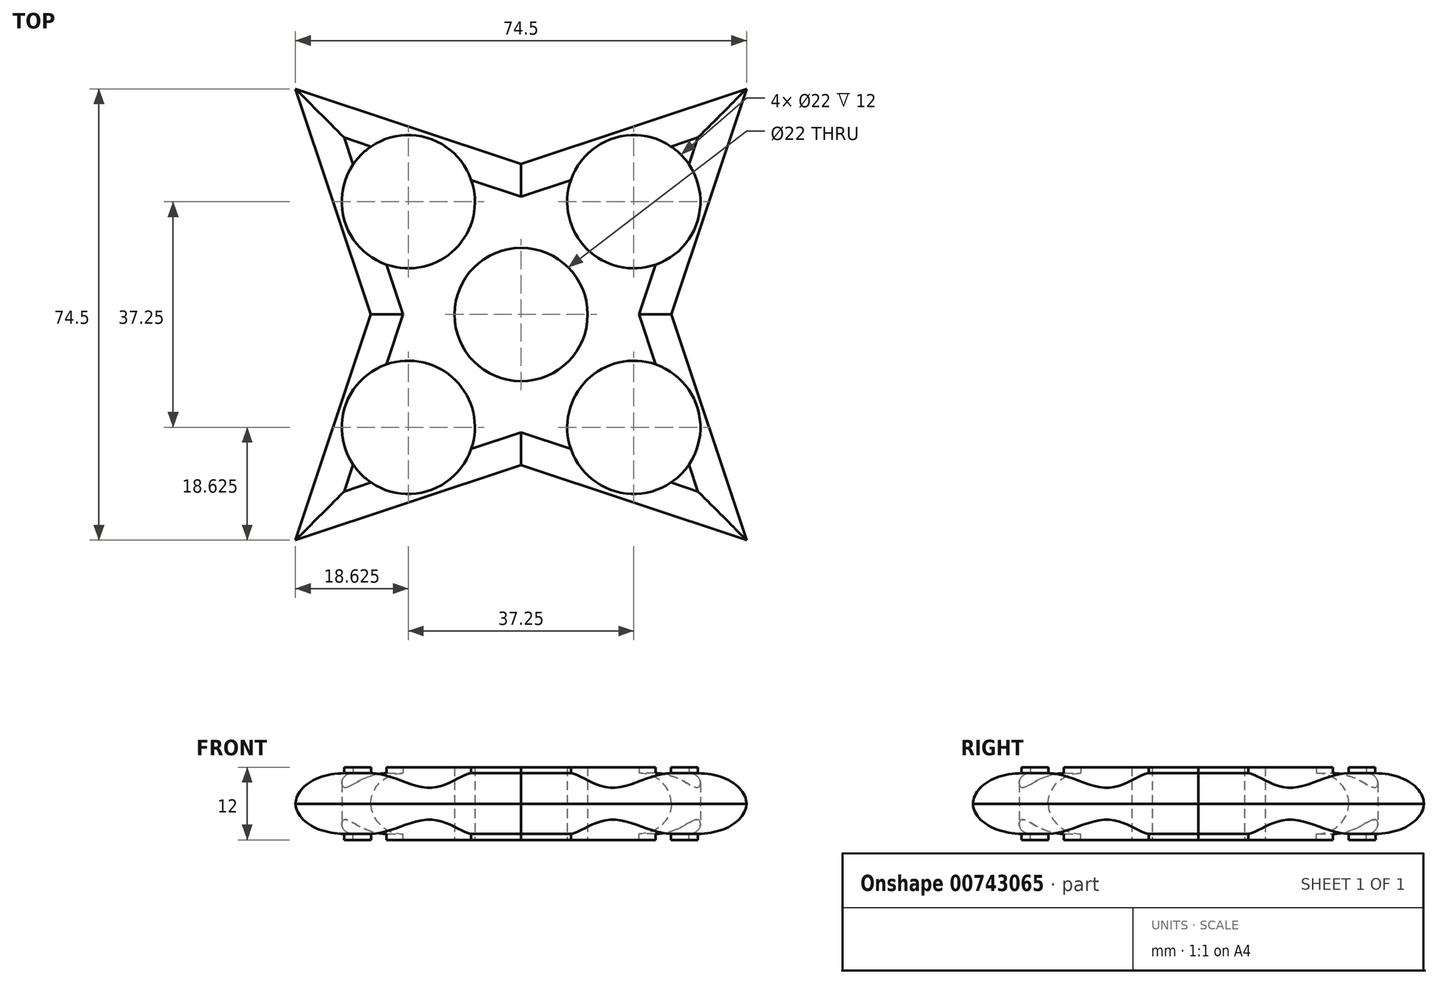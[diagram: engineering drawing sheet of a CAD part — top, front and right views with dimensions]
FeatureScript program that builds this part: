
annotation { "Feature Type Name" : "Feature", "Feature Type Description" : "" }
export const myFeature = defineFeature(function(context is Context, id is Id, definition is map)
    precondition{}
    {
        {
            var Q0;
            Q0=qCreatedBy(makeId("Top.planeOp"),FACE);
            var sketch = newSketch(context, id + "F0", { "sketchPlane" : qUnion([Q0])});
            skLineSegment(sketch, "E0.bottom", {"start": v(-109.63, 111.87) * mm, "end": v(113.44, 111.87) * mm});
            skLineSegment(sketch, "E0.top", {"start": v(-109.63, -97) * mm, "end": v(113.44, -97) * mm});
            skLineSegment(sketch, "E0.left", {"start": v(-109.63, 111.87) * mm, "end": v(-109.63, -97) * mm});
            skLineSegment(sketch, "E0.right", {"start": v(113.44, 111.87) * mm, "end": v(113.44, -97) * mm});
            skCircle(sketch, "E1", {"center": v(0, 0) * mm, "radius": 11 * mm});
            skLineSegment(sketch, "E2", {"start": v(0, 11) * mm, "end": v(0, 74.5) * mm});
            skLineSegment(sketch, "E3", {"start": v(11, 0) * mm, "end": v(74.5, 0) * mm});
            skLineSegment(sketch, "E4", {"start": v(0, -11) * mm, "end": v(0, -74.5) * mm});
            skLineSegment(sketch, "E5", {"start": v(-11, 0) * mm, "end": v(-74.5, 0) * mm});
            skLineSegment(sketch, "E6", {"start": v(37.25, 37.25) * mm, "end": v(-37.25, -37.25) * mm});
            skLineSegment(sketch, "E7", {"start": v(-37.25, 37.25) * mm, "end": v(37.25, -37.25) * mm});
            skLineSegment(sketch, "E8", {"start": v(37.25, 37.25) * mm, "end": v(0, -74.5) * mm});
            skLineSegment(sketch, "E9", {"start": v(-37.25, 37.25) * mm, "end": v(0, -74.5) * mm});
            skLineSegment(sketch, "E10", {"start": v(-74.5, 0) * mm, "end": v(37.25, 37.25) * mm});
            skLineSegment(sketch, "E11", {"start": v(37.25, -37.25) * mm, "end": v(-74.5, 0) * mm});
            skLineSegment(sketch, "E12", {"start": v(-37.25, -37.25) * mm, "end": v(0, 74.5) * mm});
            skLineSegment(sketch, "E13", {"start": v(37.25, -37.25) * mm, "end": v(0, 74.5) * mm});
            skLineSegment(sketch, "E14", {"start": v(-37.25, -37.25) * mm, "end": v(74.5, 0) * mm});
            skLineSegment(sketch, "E15", {"start": v(-37.25, 37.25) * mm, "end": v(74.5, 0) * mm});
            skCircle(sketch, "E16", {"center": v(-18.62, 18.62) * mm, "radius": 11 * mm});
            skCircle(sketch, "E17", {"center": v(18.63, 18.62) * mm, "radius": 11 * mm});
            skCircle(sketch, "E18", {"center": v(18.63, -18.62) * mm, "radius": 11 * mm});
            skCircle(sketch, "E19", {"center": v(-18.62, -18.62) * mm, "radius": 11 * mm});
            skSolve(sketch);
        }
        {
            var Q0;
            {var subQ0=sQuery(id+"F0.wireOp",EDGE,"E11");var subQ1=sQuery(id+"F0.wireOp",EDGE,"E8");var subQ2=makeQuery(id+"F0.imprint","INTERSECT",VERTEX,{"derivedFrom":[subQ1,subQ0]});Q0=makeQuery(id+"F0.imprint","IMPRINT",FACE,{"disambiguationData":[TD([[makeQuery(id+"F0.imprint","IMPRINT",EDGE,{"disambiguationData":[TD([[subQ2,1.0]])],"derivedFrom":subQ1}),-1.0]])]});}
            var Q1;
            {var subQ0=sQuery(id+"F0.wireOp",EDGE,"E14");var subQ1=sQuery(id+"F0.wireOp",EDGE,"E9");var subQ2=makeQuery(id+"F0.imprint","INTERSECT",VERTEX,{"derivedFrom":[subQ1,subQ0]});Q1=makeQuery(id+"F0.imprint","IMPRINT",FACE,{"disambiguationData":[TD([[makeQuery(id+"F0.imprint","IMPRINT",EDGE,{"disambiguationData":[TD([[subQ2,1.0]])],"derivedFrom":subQ1}),1.0]])]});}
            var Q2;
            {var subQ0=sQuery(id+"F0.wireOp",EDGE,"E4");var subQ1=sQuery(id+"F0.wireOp",EDGE,"E1");var subQ2=makeQuery(id+"F0.imprint","INTERSECT",VERTEX,{"derivedFrom":[subQ1,subQ0]});Q2=makeQuery(id+"F0.imprint","IMPRINT",FACE,{"disambiguationData":[TD([[makeQuery(id+"F0.imprint","IMPRINT",EDGE,{"disambiguationData":[TD([[subQ2,1.0]])],"derivedFrom":subQ1}),-1.0]])]});}
            var Q3;
            {var subQ0=sQuery(id+"F0.wireOp",EDGE,"E5");var subQ1=sQuery(id+"F0.wireOp",EDGE,"E1");var subQ2=makeQuery(id+"F0.imprint","INTERSECT",VERTEX,{"derivedFrom":[subQ1,subQ0]});Q3=makeQuery(id+"F0.imprint","IMPRINT",FACE,{"disambiguationData":[TD([[makeQuery(id+"F0.imprint","IMPRINT",EDGE,{"disambiguationData":[TD([[subQ2,-1.0]])],"derivedFrom":subQ1}),-1.0]])]});}
            var Q4;
            {var subQ0=sQuery(id+"F0.wireOp",EDGE,"E5");var subQ1=sQuery(id+"F0.wireOp",EDGE,"E1");var subQ2=makeQuery(id+"F0.imprint","INTERSECT",VERTEX,{"derivedFrom":[subQ1,subQ0]});Q4=makeQuery(id+"F0.imprint","IMPRINT",FACE,{"disambiguationData":[TD([[makeQuery(id+"F0.imprint","IMPRINT",EDGE,{"disambiguationData":[TD([[subQ2,1.0]])],"derivedFrom":subQ1}),-1.0]])]});}
            var Q5;
            {var subQ0=sQuery(id+"F0.wireOp",EDGE,"E2");var subQ1=sQuery(id+"F0.wireOp",EDGE,"E1");var subQ2=makeQuery(id+"F0.imprint","INTERSECT",VERTEX,{"derivedFrom":[subQ1,subQ0]});Q5=makeQuery(id+"F0.imprint","IMPRINT",FACE,{"disambiguationData":[TD([[makeQuery(id+"F0.imprint","IMPRINT",EDGE,{"disambiguationData":[TD([[subQ2,-1.0]])],"derivedFrom":subQ1}),-1.0]])]});}
            var Q6;
            {var subQ0=sQuery(id+"F0.wireOp",EDGE,"E2");var subQ1=sQuery(id+"F0.wireOp",EDGE,"E1");var subQ2=makeQuery(id+"F0.imprint","INTERSECT",VERTEX,{"derivedFrom":[subQ1,subQ0]});Q6=makeQuery(id+"F0.imprint","IMPRINT",FACE,{"disambiguationData":[TD([[makeQuery(id+"F0.imprint","IMPRINT",EDGE,{"disambiguationData":[TD([[subQ2,1.0]])],"derivedFrom":subQ1}),-1.0]])]});}
            var Q7;
            {var subQ0=sQuery(id+"F0.wireOp",EDGE,"E3");var subQ1=sQuery(id+"F0.wireOp",EDGE,"E1");var subQ2=makeQuery(id+"F0.imprint","INTERSECT",VERTEX,{"derivedFrom":[subQ1,subQ0]});Q7=makeQuery(id+"F0.imprint","IMPRINT",FACE,{"disambiguationData":[TD([[makeQuery(id+"F0.imprint","IMPRINT",EDGE,{"disambiguationData":[TD([[subQ2,-1.0]])],"derivedFrom":subQ1}),-1.0]])]});}
            var Q8;
            {var subQ0=sQuery(id+"F0.wireOp",EDGE,"E3");var subQ1=sQuery(id+"F0.wireOp",EDGE,"E1");var subQ2=makeQuery(id+"F0.imprint","INTERSECT",VERTEX,{"derivedFrom":[subQ1,subQ0]});Q8=makeQuery(id+"F0.imprint","IMPRINT",FACE,{"disambiguationData":[TD([[makeQuery(id+"F0.imprint","IMPRINT",EDGE,{"disambiguationData":[TD([[subQ2,1.0]])],"derivedFrom":subQ1}),-1.0]])]});}
            var Q9;
            {var subQ0=sQuery(id+"F0.wireOp",EDGE,"E4");var subQ1=sQuery(id+"F0.wireOp",EDGE,"E1");var subQ2=makeQuery(id+"F0.imprint","INTERSECT",VERTEX,{"derivedFrom":[subQ1,subQ0]});Q9=makeQuery(id+"F0.imprint","IMPRINT",FACE,{"disambiguationData":[TD([[makeQuery(id+"F0.imprint","IMPRINT",EDGE,{"disambiguationData":[TD([[subQ2,-1.0]])],"derivedFrom":subQ1}),-1.0]])]});}
            var Q10;
            {var subQ0=sQuery(id+"F0.wireOp",EDGE,"E13");var subQ3=sQuery(id+"F0.wireOp",EDGE,"E14");var subQ5=makeQuery(id+"F0.imprint","INTERSECT",VERTEX,{"derivedFrom":[subQ0,subQ3]});Q10=makeQuery(id+"F0.imprint","IMPRINT",FACE,{"disambiguationData":[TD([[makeQuery(id+"F0.imprint","IMPRINT",EDGE,{"disambiguationData":[TD([[subQ5,-1.0]])],"derivedFrom":subQ0}),1.0]])]});}
            var Q11;
            {var subQ0=sQuery(id+"F0.wireOp",EDGE,"E15");var subQ1=sQuery(id+"F0.wireOp",EDGE,"E8");var subQ2=makeQuery(id+"F0.imprint","INTERSECT",VERTEX,{"derivedFrom":[subQ1,subQ0]});Q11=makeQuery(id+"F0.imprint","IMPRINT",FACE,{"disambiguationData":[TD([[makeQuery(id+"F0.imprint","IMPRINT",EDGE,{"disambiguationData":[TD([[subQ2,-1.0]])],"derivedFrom":subQ1}),-1.0]])]});}
            var Q12;
            {var subQ0=sQuery(id+"F0.wireOp",EDGE,"E15");var subQ3=sQuery(id+"F0.wireOp",EDGE,"E12");var subQ5=makeQuery(id+"F0.imprint","INTERSECT",VERTEX,{"derivedFrom":[subQ3,subQ0]});Q12=makeQuery(id+"F0.imprint","IMPRINT",FACE,{"disambiguationData":[TD([[makeQuery(id+"F0.imprint","IMPRINT",EDGE,{"disambiguationData":[TD([[subQ5,1.0]])],"derivedFrom":subQ3}),-1.0]])]});}
            var Q13;
            {var subQ0=sQuery(id+"F0.wireOp",EDGE,"E13");var subQ1=sQuery(id+"F0.wireOp",EDGE,"E10");var subQ2=makeQuery(id+"F0.imprint","INTERSECT",VERTEX,{"derivedFrom":[subQ1,subQ0]});Q13=makeQuery(id+"F0.imprint","IMPRINT",FACE,{"disambiguationData":[TD([[makeQuery(id+"F0.imprint","IMPRINT",EDGE,{"disambiguationData":[TD([[subQ2,1.0]])],"derivedFrom":subQ1}),-1.0]])]});}
            var Q14;
            {var subQ0=sQuery(id+"F0.wireOp",EDGE,"E10");var subQ3=sQuery(id+"F0.wireOp",EDGE,"E13");var subQ5=makeQuery(id+"F0.imprint","INTERSECT",VERTEX,{"derivedFrom":[subQ0,subQ3]});Q14=makeQuery(id+"F0.imprint","IMPRINT",FACE,{"disambiguationData":[TD([[makeQuery(id+"F0.imprint","IMPRINT",EDGE,{"disambiguationData":[TD([[subQ5,-1.0]])],"derivedFrom":subQ0}),-1.0]])]});}
            var Q15;
            {var subQ0=sQuery(id+"F0.wireOp",EDGE,"E8");var subQ3=sQuery(id+"F0.wireOp",EDGE,"E15");var subQ5=makeQuery(id+"F0.imprint","INTERSECT",VERTEX,{"derivedFrom":[subQ0,subQ3]});Q15=makeQuery(id+"F0.imprint","IMPRINT",FACE,{"disambiguationData":[TD([[makeQuery(id+"F0.imprint","IMPRINT",EDGE,{"disambiguationData":[TD([[subQ5,1.0]])],"derivedFrom":subQ0}),-1.0]])]});}
            var Q16;
            {var subQ0=sQuery(id+"F0.wireOp",EDGE,"E11");var subQ3=sQuery(id+"F0.wireOp",EDGE,"E8");var subQ5=makeQuery(id+"F0.imprint","INTERSECT",VERTEX,{"derivedFrom":[subQ3,subQ0]});Q16=makeQuery(id+"F0.imprint","IMPRINT",FACE,{"disambiguationData":[TD([[makeQuery(id+"F0.imprint","IMPRINT",EDGE,{"disambiguationData":[TD([[subQ5,1.0]])],"derivedFrom":subQ3}),1.0]])]});}
            var Q17;
            {var subQ0=sQuery(id+"F0.wireOp",EDGE,"E13");var subQ3=sQuery(id+"F0.wireOp",EDGE,"E14");var subQ5=makeQuery(id+"F0.imprint","INTERSECT",VERTEX,{"derivedFrom":[subQ0,subQ3]});Q17=makeQuery(id+"F0.imprint","IMPRINT",FACE,{"disambiguationData":[TD([[makeQuery(id+"F0.imprint","IMPRINT",EDGE,{"disambiguationData":[TD([[subQ5,1.0]])],"derivedFrom":subQ0}),1.0]])]});}
            var Q18;
            {var subQ0=sQuery(id+"F0.wireOp",EDGE,"E14");var subQ3=sQuery(id+"F0.wireOp",EDGE,"E9");var subQ5=makeQuery(id+"F0.imprint","INTERSECT",VERTEX,{"derivedFrom":[subQ3,subQ0]});Q18=makeQuery(id+"F0.imprint","IMPRINT",FACE,{"disambiguationData":[TD([[makeQuery(id+"F0.imprint","IMPRINT",EDGE,{"disambiguationData":[TD([[subQ5,1.0]])],"derivedFrom":subQ3}),-1.0]])]});}
            var Q19;
            {var subQ0=sQuery(id+"F0.wireOp",EDGE,"E12");var subQ3=sQuery(id+"F0.wireOp",EDGE,"E11");var subQ5=makeQuery(id+"F0.imprint","INTERSECT",VERTEX,{"derivedFrom":[subQ3,subQ0]});Q19=makeQuery(id+"F0.imprint","IMPRINT",FACE,{"disambiguationData":[TD([[makeQuery(id+"F0.imprint","IMPRINT",EDGE,{"disambiguationData":[TD([[subQ5,1.0]])],"derivedFrom":subQ3}),-1.0]])]});}
            var Q20;
            {var subQ0=sQuery(id+"F0.wireOp",EDGE,"E12");var subQ3=sQuery(id+"F0.wireOp",EDGE,"E11");var subQ5=makeQuery(id+"F0.imprint","INTERSECT",VERTEX,{"derivedFrom":[subQ3,subQ0]});Q20=makeQuery(id+"F0.imprint","IMPRINT",FACE,{"disambiguationData":[TD([[makeQuery(id+"F0.imprint","IMPRINT",EDGE,{"disambiguationData":[TD([[subQ5,1.0]])],"derivedFrom":subQ3}),1.0]])]});}
            var Q21;
            {var subQ0=sQuery(id+"F0.wireOp",EDGE,"E10");var subQ1=sQuery(id+"F0.wireOp",EDGE,"E9");var subQ2=makeQuery(id+"F0.imprint","INTERSECT",VERTEX,{"derivedFrom":[subQ1,subQ0]});Q21=makeQuery(id+"F0.imprint","IMPRINT",FACE,{"disambiguationData":[TD([[makeQuery(id+"F0.imprint","IMPRINT",EDGE,{"disambiguationData":[TD([[subQ2,-1.0]])],"derivedFrom":subQ1}),1.0]])]});}
            var Q22;
            {var subQ0=sQuery(id+"F0.wireOp",EDGE,"E9");var subQ3=sQuery(id+"F0.wireOp",EDGE,"E10");var subQ5=makeQuery(id+"F0.imprint","INTERSECT",VERTEX,{"derivedFrom":[subQ0,subQ3]});Q22=makeQuery(id+"F0.imprint","IMPRINT",FACE,{"disambiguationData":[TD([[makeQuery(id+"F0.imprint","IMPRINT",EDGE,{"disambiguationData":[TD([[subQ5,1.0]])],"derivedFrom":subQ0}),1.0]])]});}
            var Q23;
            {var subQ0=sQuery(id+"F0.wireOp",EDGE,"E15");var subQ3=sQuery(id+"F0.wireOp",EDGE,"E12");var subQ5=makeQuery(id+"F0.imprint","INTERSECT",VERTEX,{"derivedFrom":[subQ3,subQ0]});Q23=makeQuery(id+"F0.imprint","IMPRINT",FACE,{"disambiguationData":[TD([[makeQuery(id+"F0.imprint","IMPRINT",EDGE,{"disambiguationData":[TD([[subQ5,1.0]])],"derivedFrom":subQ3}),1.0]])]});}
            extrude(context, id + "F1", {"entities" : qUnion([Q0, Q1, Q2, Q3, Q4, Q5, Q6, Q7, Q8, Q9, Q10, Q11, Q12, Q13, Q14, Q15, Q16, Q17, Q18, Q19, Q20, Q21, Q22, Q23]), "depth" : 10 * mm, "offsetDistance" : 25.4 * mm});
        }
        {
            var Q0;
            Q0=makeQuery(id+"F1.opExtrude","CAP_EDGE",EDGE,{"disambiguationData":[OSD([sQuery(id+"F0.wireOp",EDGE,"E12")])],"isStart":false});
            var Q1;
            Q1=makeQuery(id+"F1.opExtrude","CAP_EDGE",EDGE,{"disambiguationData":[OSD([sQuery(id+"F0.wireOp",EDGE,"E9")])],"isStart":false});
            var Q2;
            Q2=makeQuery(id+"F1.opExtrude","CAP_EDGE",EDGE,{"disambiguationData":[OSD([sQuery(id+"F0.wireOp",EDGE,"E14")])],"isStart":false});
            var Q3;
            Q3=makeQuery(id+"F1.opExtrude","CAP_EDGE",EDGE,{"disambiguationData":[OSD([sQuery(id+"F0.wireOp",EDGE,"E11")])],"isStart":false});
            var Q4;
            Q4=makeQuery(id+"F1.opExtrude","CAP_EDGE",EDGE,{"disambiguationData":[OSD([sQuery(id+"F0.wireOp",EDGE,"E13")])],"isStart":false});
            var Q5;
            Q5=makeQuery(id+"F1.opExtrude","CAP_EDGE",EDGE,{"disambiguationData":[OSD([sQuery(id+"F0.wireOp",EDGE,"E8")])],"isStart":false});
            var Q6;
            Q6=makeQuery(id+"F1.opExtrude","CAP_EDGE",EDGE,{"disambiguationData":[OSD([sQuery(id+"F0.wireOp",EDGE,"E10")])],"isStart":false});
            var Q7;
            Q7=makeQuery(id+"F1.opExtrude","CAP_EDGE",EDGE,{"disambiguationData":[OSD([sQuery(id+"F0.wireOp",EDGE,"E15")])],"isStart":false});
            fillet(context, id + "F2", {"entities" : qUnion([Q0, Q1, Q2, Q3, Q4, Q5, Q6, Q7]), "radius" : 5.08 * mm, "tangentPropagation" : true, "allowEdgeOverflow" : false});
        }
        {
            var Q0;
            Q0=makeQuery(id+"F1.opExtrude","CAP_EDGE",EDGE,{"disambiguationData":[OSD([sQuery(id+"F0.wireOp",EDGE,"E10")])],"isStart":true});
            var Q1;
            Q1=makeQuery(id+"F1.opExtrude","CAP_EDGE",EDGE,{"disambiguationData":[OSD([sQuery(id+"F0.wireOp",EDGE,"E8")])],"isStart":true});
            var Q2;
            Q2=makeQuery(id+"F1.opExtrude","CAP_EDGE",EDGE,{"disambiguationData":[OSD([sQuery(id+"F0.wireOp",EDGE,"E13")])],"isStart":true});
            var Q3;
            Q3=makeQuery(id+"F1.opExtrude","CAP_EDGE",EDGE,{"disambiguationData":[OSD([sQuery(id+"F0.wireOp",EDGE,"E11")])],"isStart":true});
            var Q4;
            Q4=makeQuery(id+"F1.opExtrude","CAP_EDGE",EDGE,{"disambiguationData":[OSD([sQuery(id+"F0.wireOp",EDGE,"E14")])],"isStart":true});
            var Q5;
            Q5=makeQuery(id+"F1.opExtrude","CAP_EDGE",EDGE,{"disambiguationData":[OSD([sQuery(id+"F0.wireOp",EDGE,"E12")])],"isStart":true});
            var Q6;
            Q6=makeQuery(id+"F1.opExtrude","CAP_EDGE",EDGE,{"disambiguationData":[OSD([sQuery(id+"F0.wireOp",EDGE,"E9")])],"isStart":true});
            var Q7;
            Q7=makeQuery(id+"F1.opExtrude","CAP_EDGE",EDGE,{"disambiguationData":[OSD([sQuery(id+"F0.wireOp",EDGE,"E15")])],"isStart":true});
            fillet(context, id + "F3", {"entities" : qUnion([Q0, Q1, Q2, Q3, Q4, Q5, Q6, Q7]), "radius" : 5.08 * mm, "tangentPropagation" : true, "allowEdgeOverflow" : false});
        }
        {
            var Q0;
            Q0=makeQuery(id+"F2.opFillet","SPLIT",FACE,{"disambiguationData":[OD(2.0)],"derivedFrom":makeQuery(id+"F1.opExtrude","CAP_FACE",FACE,{"disambiguationData":[OSD([sQuery(id+"F0.wireOp",EDGE,"E1"),sQuery(id+"F0.wireOp",EDGE,"E8"),sQuery(id+"F0.wireOp",EDGE,"E9"),sQuery(id+"F0.wireOp",EDGE,"E10"),sQuery(id+"F0.wireOp",EDGE,"E11"),sQuery(id+"F0.wireOp",EDGE,"E12"),sQuery(id+"F0.wireOp",EDGE,"E13"),sQuery(id+"F0.wireOp",EDGE,"E14"),sQuery(id+"F0.wireOp",EDGE,"E15"),sQuery(id+"F0.wireOp",EDGE,"E16"),sQuery(id+"F0.wireOp",EDGE,"E17"),sQuery(id+"F0.wireOp",EDGE,"E18"),sQuery(id+"F0.wireOp",EDGE,"E19")])],"isStart":false})});
            var Q1;
            Q1=makeQuery(id+"F2.opFillet","SPLIT",FACE,{"disambiguationData":[OD(1.0)],"derivedFrom":makeQuery(id+"F1.opExtrude","CAP_FACE",FACE,{"disambiguationData":[OSD([sQuery(id+"F0.wireOp",EDGE,"E1"),sQuery(id+"F0.wireOp",EDGE,"E8"),sQuery(id+"F0.wireOp",EDGE,"E9"),sQuery(id+"F0.wireOp",EDGE,"E10"),sQuery(id+"F0.wireOp",EDGE,"E11"),sQuery(id+"F0.wireOp",EDGE,"E12"),sQuery(id+"F0.wireOp",EDGE,"E13"),sQuery(id+"F0.wireOp",EDGE,"E14"),sQuery(id+"F0.wireOp",EDGE,"E15"),sQuery(id+"F0.wireOp",EDGE,"E16"),sQuery(id+"F0.wireOp",EDGE,"E17"),sQuery(id+"F0.wireOp",EDGE,"E18"),sQuery(id+"F0.wireOp",EDGE,"E19")])],"isStart":false})});
            var Q2;
            Q2=makeQuery(id+"F2.opFillet","SPLIT",FACE,{"disambiguationData":[OD(3.0)],"derivedFrom":makeQuery(id+"F1.opExtrude","CAP_FACE",FACE,{"disambiguationData":[OSD([sQuery(id+"F0.wireOp",EDGE,"E1"),sQuery(id+"F0.wireOp",EDGE,"E8"),sQuery(id+"F0.wireOp",EDGE,"E9"),sQuery(id+"F0.wireOp",EDGE,"E10"),sQuery(id+"F0.wireOp",EDGE,"E11"),sQuery(id+"F0.wireOp",EDGE,"E12"),sQuery(id+"F0.wireOp",EDGE,"E13"),sQuery(id+"F0.wireOp",EDGE,"E14"),sQuery(id+"F0.wireOp",EDGE,"E15"),sQuery(id+"F0.wireOp",EDGE,"E16"),sQuery(id+"F0.wireOp",EDGE,"E17"),sQuery(id+"F0.wireOp",EDGE,"E18"),sQuery(id+"F0.wireOp",EDGE,"E19")])],"isStart":false})});
            var Q3;
            Q3=makeQuery(id+"F2.opFillet","SPLIT",FACE,{"disambiguationData":[OD(0.0)],"derivedFrom":makeQuery(id+"F1.opExtrude","CAP_FACE",FACE,{"disambiguationData":[OSD([sQuery(id+"F0.wireOp",EDGE,"E1"),sQuery(id+"F0.wireOp",EDGE,"E8"),sQuery(id+"F0.wireOp",EDGE,"E9"),sQuery(id+"F0.wireOp",EDGE,"E10"),sQuery(id+"F0.wireOp",EDGE,"E11"),sQuery(id+"F0.wireOp",EDGE,"E12"),sQuery(id+"F0.wireOp",EDGE,"E13"),sQuery(id+"F0.wireOp",EDGE,"E14"),sQuery(id+"F0.wireOp",EDGE,"E15"),sQuery(id+"F0.wireOp",EDGE,"E16"),sQuery(id+"F0.wireOp",EDGE,"E17"),sQuery(id+"F0.wireOp",EDGE,"E18"),sQuery(id+"F0.wireOp",EDGE,"E19")])],"isStart":false})});
            var Q4;
            Q4=makeQuery(id+"F2.opFillet","SPLIT",FACE,{"disambiguationData":[OD(4.0)],"derivedFrom":makeQuery(id+"F1.opExtrude","CAP_FACE",FACE,{"disambiguationData":[OSD([sQuery(id+"F0.wireOp",EDGE,"E1"),sQuery(id+"F0.wireOp",EDGE,"E8"),sQuery(id+"F0.wireOp",EDGE,"E9"),sQuery(id+"F0.wireOp",EDGE,"E10"),sQuery(id+"F0.wireOp",EDGE,"E11"),sQuery(id+"F0.wireOp",EDGE,"E12"),sQuery(id+"F0.wireOp",EDGE,"E13"),sQuery(id+"F0.wireOp",EDGE,"E14"),sQuery(id+"F0.wireOp",EDGE,"E15"),sQuery(id+"F0.wireOp",EDGE,"E16"),sQuery(id+"F0.wireOp",EDGE,"E17"),sQuery(id+"F0.wireOp",EDGE,"E18"),sQuery(id+"F0.wireOp",EDGE,"E19")])],"isStart":false})});
            extrude(context, id + "F4", {"entities" : qUnion([Q0, Q1, Q2, Q3, Q4]), "operationType" : NewBodyOperationType.ADD, "depth" : 1 * mm, "offsetDistance" : 25.4 * mm});
        }
        {
            var Q0;
            Q0=makeQuery(id+"F3.opFillet","SPLIT",FACE,{"disambiguationData":[OD(2.0)],"derivedFrom":makeQuery(id+"F1.opExtrude","CAP_FACE",FACE,{"disambiguationData":[OSD([sQuery(id+"F0.wireOp",EDGE,"E1"),sQuery(id+"F0.wireOp",EDGE,"E8"),sQuery(id+"F0.wireOp",EDGE,"E9"),sQuery(id+"F0.wireOp",EDGE,"E10"),sQuery(id+"F0.wireOp",EDGE,"E11"),sQuery(id+"F0.wireOp",EDGE,"E12"),sQuery(id+"F0.wireOp",EDGE,"E13"),sQuery(id+"F0.wireOp",EDGE,"E14"),sQuery(id+"F0.wireOp",EDGE,"E15"),sQuery(id+"F0.wireOp",EDGE,"E16"),sQuery(id+"F0.wireOp",EDGE,"E17"),sQuery(id+"F0.wireOp",EDGE,"E18"),sQuery(id+"F0.wireOp",EDGE,"E19")])],"isStart":true})});
            var Q1;
            Q1=makeQuery(id+"F3.opFillet","SPLIT",FACE,{"disambiguationData":[OD(3.0)],"derivedFrom":makeQuery(id+"F1.opExtrude","CAP_FACE",FACE,{"disambiguationData":[OSD([sQuery(id+"F0.wireOp",EDGE,"E1"),sQuery(id+"F0.wireOp",EDGE,"E8"),sQuery(id+"F0.wireOp",EDGE,"E9"),sQuery(id+"F0.wireOp",EDGE,"E10"),sQuery(id+"F0.wireOp",EDGE,"E11"),sQuery(id+"F0.wireOp",EDGE,"E12"),sQuery(id+"F0.wireOp",EDGE,"E13"),sQuery(id+"F0.wireOp",EDGE,"E14"),sQuery(id+"F0.wireOp",EDGE,"E15"),sQuery(id+"F0.wireOp",EDGE,"E16"),sQuery(id+"F0.wireOp",EDGE,"E17"),sQuery(id+"F0.wireOp",EDGE,"E18"),sQuery(id+"F0.wireOp",EDGE,"E19")])],"isStart":true})});
            var Q2;
            Q2=makeQuery(id+"F3.opFillet","SPLIT",FACE,{"disambiguationData":[OD(0.0)],"derivedFrom":makeQuery(id+"F1.opExtrude","CAP_FACE",FACE,{"disambiguationData":[OSD([sQuery(id+"F0.wireOp",EDGE,"E1"),sQuery(id+"F0.wireOp",EDGE,"E8"),sQuery(id+"F0.wireOp",EDGE,"E9"),sQuery(id+"F0.wireOp",EDGE,"E10"),sQuery(id+"F0.wireOp",EDGE,"E11"),sQuery(id+"F0.wireOp",EDGE,"E12"),sQuery(id+"F0.wireOp",EDGE,"E13"),sQuery(id+"F0.wireOp",EDGE,"E14"),sQuery(id+"F0.wireOp",EDGE,"E15"),sQuery(id+"F0.wireOp",EDGE,"E16"),sQuery(id+"F0.wireOp",EDGE,"E17"),sQuery(id+"F0.wireOp",EDGE,"E18"),sQuery(id+"F0.wireOp",EDGE,"E19")])],"isStart":true})});
            var Q3;
            Q3=makeQuery(id+"F3.opFillet","SPLIT",FACE,{"disambiguationData":[OD(1.0)],"derivedFrom":makeQuery(id+"F1.opExtrude","CAP_FACE",FACE,{"disambiguationData":[OSD([sQuery(id+"F0.wireOp",EDGE,"E1"),sQuery(id+"F0.wireOp",EDGE,"E8"),sQuery(id+"F0.wireOp",EDGE,"E9"),sQuery(id+"F0.wireOp",EDGE,"E10"),sQuery(id+"F0.wireOp",EDGE,"E11"),sQuery(id+"F0.wireOp",EDGE,"E12"),sQuery(id+"F0.wireOp",EDGE,"E13"),sQuery(id+"F0.wireOp",EDGE,"E14"),sQuery(id+"F0.wireOp",EDGE,"E15"),sQuery(id+"F0.wireOp",EDGE,"E16"),sQuery(id+"F0.wireOp",EDGE,"E17"),sQuery(id+"F0.wireOp",EDGE,"E18"),sQuery(id+"F0.wireOp",EDGE,"E19")])],"isStart":true})});
            var Q4;
            Q4=makeQuery(id+"F3.opFillet","SPLIT",FACE,{"disambiguationData":[OD(4.0)],"derivedFrom":makeQuery(id+"F1.opExtrude","CAP_FACE",FACE,{"disambiguationData":[OSD([sQuery(id+"F0.wireOp",EDGE,"E1"),sQuery(id+"F0.wireOp",EDGE,"E8"),sQuery(id+"F0.wireOp",EDGE,"E9"),sQuery(id+"F0.wireOp",EDGE,"E10"),sQuery(id+"F0.wireOp",EDGE,"E11"),sQuery(id+"F0.wireOp",EDGE,"E12"),sQuery(id+"F0.wireOp",EDGE,"E13"),sQuery(id+"F0.wireOp",EDGE,"E14"),sQuery(id+"F0.wireOp",EDGE,"E15"),sQuery(id+"F0.wireOp",EDGE,"E16"),sQuery(id+"F0.wireOp",EDGE,"E17"),sQuery(id+"F0.wireOp",EDGE,"E18"),sQuery(id+"F0.wireOp",EDGE,"E19")])],"isStart":true})});
            extrude(context, id + "F5", {"entities" : qUnion([Q0, Q1, Q2, Q3, Q4]), "operationType" : NewBodyOperationType.ADD, "depth" : 1 * mm, "offsetDistance" : 25.4 * mm});
        }
    });
